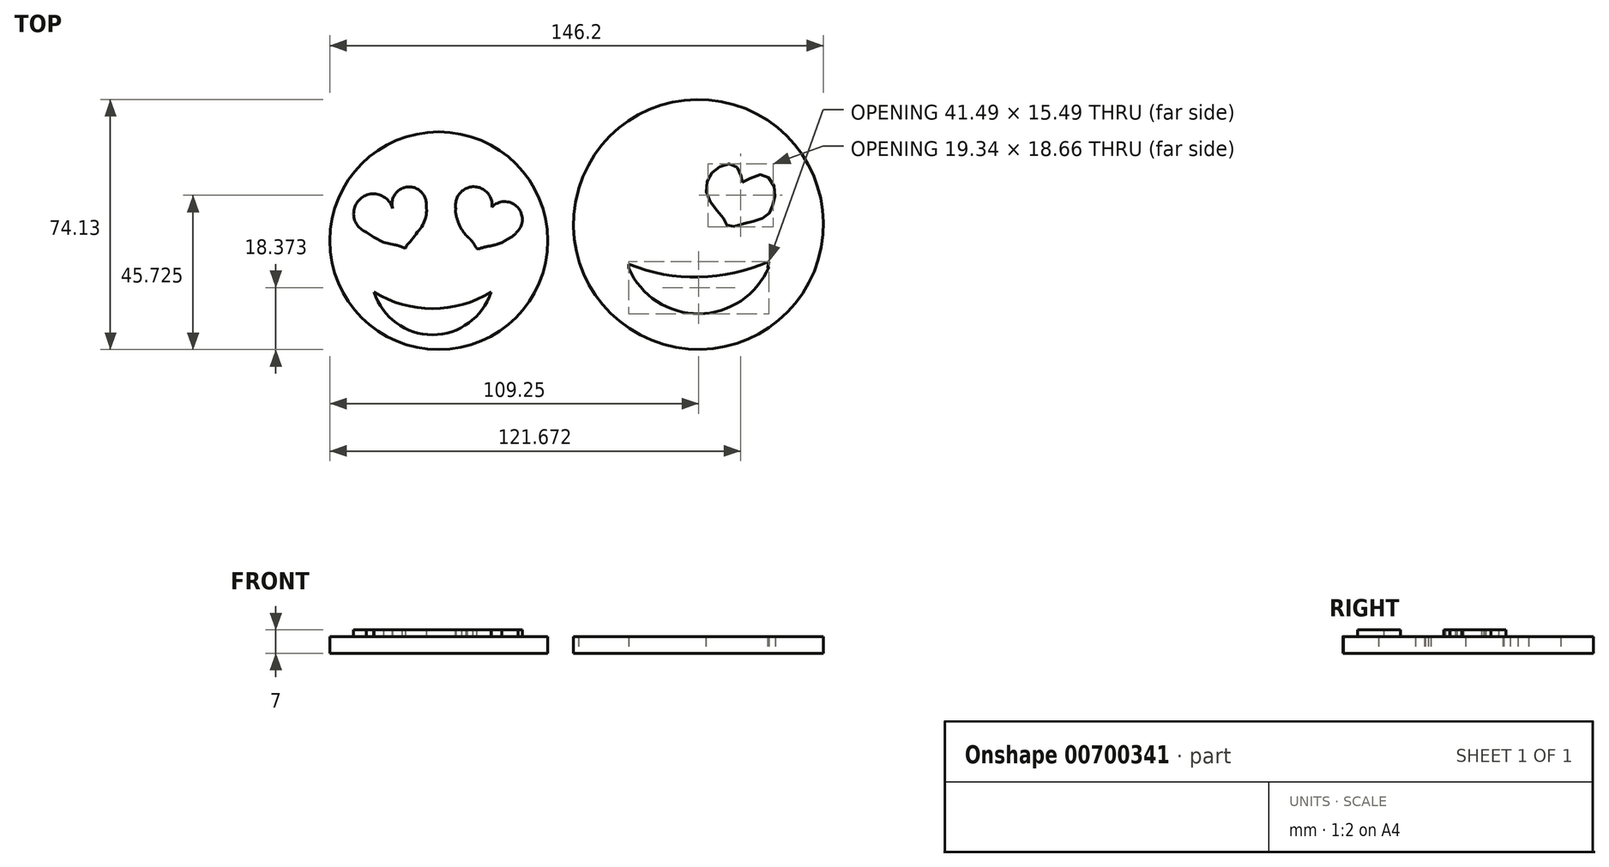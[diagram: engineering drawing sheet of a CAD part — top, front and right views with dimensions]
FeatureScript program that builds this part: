
annotation { "Feature Type Name" : "Feature", "Feature Type Description" : "" }
export const myFeature = defineFeature(function(context is Context, id is Id, definition is map)
    precondition{}
    {
        {
            var Q0;
            Q0=qCreatedBy(makeId("Top.planeOp"),FACE);
            var sketch = newSketch(context, id + "F0", { "sketchPlane" : qUnion([Q0])});
            skCircle(sketch, "E0", {"center": v(38.32, 42.05) * mm, "radius": 37.01 * mm});
            skPoint(sketch, "E1.right.end.orphan", {"position": v(22.14, 44.9) * mm});
            skLineSegment(sketch, "E2.left", {"start": v(17.7, 44.9) * mm, "end": v(17.7, 44.9) * mm});
            skLineSegment(sketch, "E2.right", {"start": v(-10.58, 44.9) * mm, "end": v(-10.58, 44.9) * mm});
            skLineSegment(sketch, "E3.right", {"start": v(2.76, 52.31) * mm, "end": v(2.76, 52.54) * mm});
            skLineSegment(sketch, "E4.bottom", {"start": v(2.82, 52.54) * mm, "end": v(2.76, 52.54) * mm});
            skPoint(sketch, "E5.center.orphan", {"position": v(22.14, 56.45) * mm});
            skPoint(sketch, "E6.center.orphan", {"position": v(12.71, 56.45) * mm});
            skPoint(sketch, "E7.11.internal.orphan", {"position": v(32.45, 56.45) * mm});
            skPoint(sketch, "E7.5.internal.orphan", {"position": v(12.71, 52.9) * mm});
            skPoint(sketch, "E7.8.internal.orphan", {"position": v(22.14, 40.98) * mm});
            skPoint(sketch, "E8.start.orphan", {"position": v(23.74, 28.54) * mm});
            skPoint(sketch, "E9.start.orphan", {"position": v(21.25, 28.54) * mm});
            skPoint(sketch, "E10.1.internal.orphan", {"position": v(21.25, 21.42) * mm});
            skArc(sketch, "E11", {"start": v(17.64, 29.07) * mm, "mid": v(38.48, 15.56) * mm, "end": v(59.12, 29.37) * mm});
            skLineSegment(sketch, "E12", {"start": v(17.64, 29.07) * mm, "end": v(18.85, 29.07) * mm});
            skArc(sketch, "E13", {"start": v(58.75, 29.07) * mm, "mid": v(58.94, 29.22) * mm, "end": v(59.12, 29.37) * mm});
            skLineSegment(sketch, "E14.trimOffspring", {"start": v(58.75, 29.07) * mm, "end": v(59, 29.07) * mm});
            skPoint(sketch, "E15.center.orphan", {"position": v(37.78, 69.25) * mm});
            skArc(sketch, "E16", {"start": v(17.64, 30.27) * mm, "mid": v(38.46, 26.4) * mm, "end": v(59.12, 31.05) * mm});
            skLineSegment(sketch, "E17", {"start": v(58.75, 29.07) * mm, "end": v(59.12, 31.05) * mm});
            skLineSegment(sketch, "E18", {"start": v(17.64, 29.07) * mm, "end": v(17.64, 30.27) * mm});
            skPoint(sketch, "E19.0.internal.orphan", {"position": v(55.2, 56.45) * mm});
            skPoint(sketch, "E19.10.internal.orphan", {"position": v(66.23, 56.45) * mm});
            skPoint(sketch, "E19.3.internal.orphan", {"position": v(44.54, 52.9) * mm});
            skPoint(sketch, "E19.5.internal.orphan", {"position": v(49.52, 44.9) * mm});
            skPoint(sketch, "E19.6.internal.orphan", {"position": v(53.07, 40.98) * mm});
            skPoint(sketch, "E19.7.internal.orphan", {"position": v(58.94, 44.9) * mm});
            skPoint(sketch, "E19.9.internal.orphan", {"position": v(65.34, 52.9) * mm});
            skPoint(sketch, "E20.11.internal.orphan", {"position": v(32.45, 51.12) * mm});
            skPoint(sketch, "E20.13.internal.orphan", {"position": v(32.45, 60.19) * mm});
            skPoint(sketch, "E20.9.internal.orphan", {"position": v(27.47, 44.9) * mm});
            skFitSpline(sketch, "E21", {"points": [v(21.47, 54.66) * mm, v(20.2, 55.55) * mm, v(18.18, 56.53) * mm, v(15.86, 56.53) * mm, v(13.7, 55.48) * mm, v(12.71, 53.69) * mm, v(12.71, 51.75) * mm], "startDerivative": vector(-8.2, 6.07) * mm, "endDerivative": vector(1.18, -12.09) * mm});
            skFitSpline(sketch, "E22", {"points": [v(32.28, 52.9) * mm, v(32.45, 54.07) * mm, v(31.43, 56.45) * mm, v(30.06, 58.5) * mm, v(28.47, 59.57) * mm, v(25.83, 59.99) * mm, v(23.09, 58.5) * mm, v(22.14, 56.45) * mm, v(21.07, 54.95) * mm], "startDerivative": vector(3.78, 11.78) * mm, "endDerivative": vector(-10.45, -12.22) * mm});
            skFitSpline(sketch, "E23", {"points": [v(12.71, 51.75) * mm, v(12.71, 50.37) * mm, v(12.71, 48.79) * mm, v(13.58, 46.89) * mm, v(16.22, 44.9) * mm, v(21.07, 42.98) * mm, v(24.35, 42.13) * mm, v(26.26, 41.18) * mm], "startDerivative": vector(0.32, -13.04) * mm, "endDerivative": vector(13.75, -8.08) * mm});
            skPoint(sketch, "E24.1.internal.orphan", {"position": v(32.45, 49.18) * mm});
            skFitSpline(sketch, "E25", {"points": [v(26.26, 41.18) * mm, v(29.1, 44.9) * mm, v(32.45, 49.18) * mm, v(32.4, 53.25) * mm], "startDerivative": vector(7.72, 11.06) * mm, "endDerivative": vector(-2.6, 13.4) * mm});
            skFitSpline(sketch, "E26", {"points": [v(51.26, 54.53) * mm, v(50.9, 56.45) * mm, v(48.86, 59.7) * mm, v(44.98, 59.33) * mm, v(41.66, 56.45) * mm, v(40.55, 51.95) * mm, v(43.14, 46.96) * mm, v(45.9, 43.45) * mm, v(47.2, 41.42) * mm, v(51.45, 42.16) * mm, v(55.2, 43.08) * mm, v(58.94, 44.9) * mm, v(60.3, 47.88) * mm, v(61.05, 51.95) * mm, v(58.94, 56.1) * mm, v(55.2, 56.45) * mm, v(51.26, 54.53) * mm]});
            skFitSpline(sketch, "E27", {"points": [v(60.68, 36.44) * mm, v(61.6, 36.44) * mm, v(74.7, 29.42) * mm], "startDerivative": vector(3.46, 0.87) * mm, "endDerivative": vector(21.08, -12.27) * mm});
            skCircle(sketch, "E28", {"center": v(-38.61, 37.19) * mm, "radius": 32.26 * mm});
            skSolve(sketch);
        }
        {
            var Q0;
            Q0 = qSketchRegion(id + "F0", true);
            extrude(context, id + "F1", {"entities" : qUnion([Q0]), "depth" : 5 * mm, "offsetDistance" : 25.4 * mm});
        }
        {
            var Q0;
            Q0=makeQuery(id+"F1.opExtrude","CAP_FACE",FACE,{"disambiguationData":[OSD([sQuery(id+"F0.wireOp",EDGE,"E28")])],"isStart":false});
            var sketch = newSketch(context, id + "F2", { "sketchPlane" : qUnion([Q0])});
            skArc(sketch, "E29", {"start": v(-22.87, 47.18) * mm, "mid": v(-28.51, 53.19) * mm, "end": v(-33.52, 46.64) * mm});
            skArc(sketch, "E30", {"start": v(-15.07, 40.2) * mm, "mid": v(-15.6, 47.46) * mm, "end": v(-22.87, 47.18) * mm});
            skFitSpline(sketch, "E31", {"points": [v(-21.25, 36.18) * mm, v(-19.9, 36.65) * mm, v(-18.55, 37.45) * mm, v(-16.75, 38.53) * mm, v(-15.07, 40.2) * mm], "startDerivative": vector(6.32, 1.75) * mm, "endDerivative": vector(5.64, 6.42) * mm});
            skFitSpline(sketch, "E32", {"points": [v(-27.45, 34.94) * mm, v(-28.61, 36.83) * mm, v(-30.14, 38.44) * mm, v(-31.85, 40.6) * mm, v(-33.29, 44.02) * mm, v(-33.7, 46.09) * mm], "startDerivative": vector(-5.8, 10.59) * mm, "endDerivative": vector(-1.6, 10.56) * mm});
            skFitSpline(sketch, "E33", {"points": [v(-42.35, 48.54) * mm, v(-42.21, 46.09) * mm, v(-42.34, 44.6) * mm, v(-42.68, 43.46) * mm, v(-43.53, 41.68) * mm, v(-44.5, 40.32) * mm, v(-45.69, 38.75) * mm, v(-46.92, 37.14) * mm, v(-48.2, 35.66) * mm, v(-48.49, 35.02) * mm, v(-49.84, 35.49) * mm, v(-51.63, 36) * mm, v(-53.36, 36.38) * mm, v(-54.98, 36.76) * mm, v(-57.27, 37.6) * mm, v(-58.62, 38.24) * mm, v(-60.28, 39.52) * mm, v(-61.04, 40.63) * mm], "startDerivative": vector(2.92, -36.65) * mm, "endDerivative": vector(-11.74, 21.15) * mm});
            skArc(sketch, "E34", {"start": v(-60.03, 39.75) * mm, "mid": v(-60, 39.72) * mm, "end": v(-59.96, 39.7) * mm});
            skLineSegment(sketch, "E35", {"start": v(-59.96, 39.7) * mm, "end": v(-59.98, 39.69) * mm});
            skPoint(sketch, "E36.orphan", {"position": v(-64.44, 35.02) * mm});
            skPoint(sketch, "E37.orphan", {"position": v(-59.47, 42.52) * mm});
            skLineSegment(sketch, "E38", {"start": v(-60.03, 39.75) * mm, "end": v(-60.03, 39.74) * mm});
            skPoint(sketch, "E39.orphan", {"position": v(-58.62, 41.1) * mm});
            skPoint(sketch, "E40.center.orphan", {"position": v(-54.76, 41.1) * mm});
            skPoint(sketch, "E41.orphan", {"position": v(-66.52, 38.24) * mm});
            skPoint(sketch, "E42.center.orphan", {"position": v(-54.76, 42.52) * mm});
            skArc(sketch, "E43", {"start": v(-60.03, 39.74) * mm, "mid": v(-60, 39.71) * mm, "end": v(-59.98, 39.69) * mm});
            skArc(sketch, "E44", {"start": v(-59.65, 38.89) * mm, "mid": v(-59.6, 38.88) * mm, "end": v(-59.56, 38.87) * mm});
            skLineSegment(sketch, "E45", {"start": v(-59.9, 39.16) * mm, "end": v(-59.92, 39.14) * mm});
            skPoint(sketch, "E46.orphan", {"position": v(-64.44, 32.28) * mm});
            skPoint(sketch, "E47.center.orphan", {"position": v(-56.65, 45.56) * mm});
            skPoint(sketch, "E48.center.orphan", {"position": v(-57.78, 44.49) * mm});
            skPoint(sketch, "E49.center.orphan", {"position": v(-54.76, 44.49) * mm});
            skPoint(sketch, "E50.center.orphan", {"position": v(-55.74, 44.49) * mm});
            skPoint(sketch, "E51.center.orphan", {"position": v(-47.36, 47.8) * mm});
            skArc(sketch, "E52", {"start": v(-52.29, 46.77) * mm, "mid": v(-61.93, 49.54) * mm, "end": v(-59.96, 39.7) * mm});
            skArc(sketch, "E53", {"start": v(-42.35, 48.54) * mm, "mid": v(-48.29, 53.1) * mm, "end": v(-52.29, 46.77) * mm});
            skLineSegment(sketch, "E54", {"start": v(-33.7, 46.09) * mm, "end": v(-33.52, 46.64) * mm});
            skLineSegment(sketch, "E55", {"start": v(-33.52, 46.64) * mm, "end": v(-33.7, 46.09) * mm});
            skPoint(sketch, "E56.orphan", {"position": v(-27.45, 38.43) * mm});
            skFitSpline(sketch, "E57.trimOffspring", {"points": [v(-33.52, 46.64) * mm, v(-33.83, 44.91) * mm, v(-32.93, 42.58) * mm, v(-31.85, 40.6) * mm, v(-30.14, 38.44) * mm, v(-28.61, 36.83) * mm, v(-27.45, 34.94) * mm, v(-25.1, 35.3) * mm, v(-22.41, 35.84) * mm, v(-19.9, 36.65) * mm, v(-17.47, 37.54) * mm, v(-15.4, 39.34) * mm, v(-15.07, 40.2) * mm], "startDerivative": vector(-7.78, -22.58) * mm, "endDerivative": vector(3.17, 15.14) * mm});
            skPoint(sketch, "E58.end.orphan", {"position": v(-27.8, 35.26) * mm});
            skLineSegment(sketch, "E59", {"start": v(-42.35, 48.54) * mm, "end": v(-42.28, 47.68) * mm});
            skPoint(sketch, "E60.center.orphan", {"position": v(-47.36, 46.09) * mm});
            skPoint(sketch, "E61.center.orphan", {"position": v(-56.76, 42.52) * mm});
            skArc(sketch, "E62", {"start": v(-57.76, 21.94) * mm, "mid": v(-40.46, 9.33) * mm, "end": v(-23.16, 21.94) * mm});
            skArc(sketch, "E63", {"start": v(-57.76, 21.94) * mm, "mid": v(-40.46, 17.09) * mm, "end": v(-23.16, 21.94) * mm});
            skLineSegment(sketch, "E64", {"start": v(-59.96, 39.7) * mm, "end": v(-57.86, 38.24) * mm});
            skLineSegment(sketch, "E65", {"start": v(-57.86, 38.24) * mm, "end": v(-54.98, 36.76) * mm});
            skLineSegment(sketch, "E66", {"start": v(-54.98, 36.76) * mm, "end": v(-51.63, 36) * mm});
            skLineSegment(sketch, "E67", {"start": v(-51.63, 36) * mm, "end": v(-48.49, 35.02) * mm});
            skSolve(sketch);
        }
        {
            var Q0;
            Q0=makeQuery(id+"F2.imprint","IMPRINT",FACE,{"disambiguationData":[TD([[makeQuery(id+"F2.imprint","IMPRINT",EDGE,{"derivedFrom":sQuery(id+"F2.wireOp",EDGE,"E29")}),1.0]])]});
            extrude(context, id + "F3", {"entities" : qUnion([Q0]), "operationType" : NewBodyOperationType.ADD, "depth" : 2 * mm, "offsetDistance" : 25 * mm});
        }
        {
            var Q0;
            Q0=makeQuery(id+"F2.imprint","IMPRINT",FACE,{"disambiguationData":[TD([[makeQuery(id+"F2.imprint","IMPRINT",EDGE,{"derivedFrom":sQuery(id+"F2.wireOp",EDGE,"E34")}),1.0]])]});
            extrude(context, id + "F4", {"entities" : qUnion([Q0]), "operationType" : NewBodyOperationType.ADD, "depth" : 2 * mm, "offsetDistance" : 25 * mm});
        }
        {
            var Q0;
            Q0=makeQuery(id+"F2.imprint","IMPRINT",FACE,{"disambiguationData":[TD([[makeQuery(id+"F2.imprint","IMPRINT",EDGE,{"derivedFrom":sQuery(id+"F2.wireOp",EDGE,"E62")}),1.0]])]});
            extrude(context, id + "F5", {"entities" : qUnion([Q0]), "operationType" : NewBodyOperationType.ADD, "depth" : 2 * mm, "offsetDistance" : 25 * mm});
        }
    });
